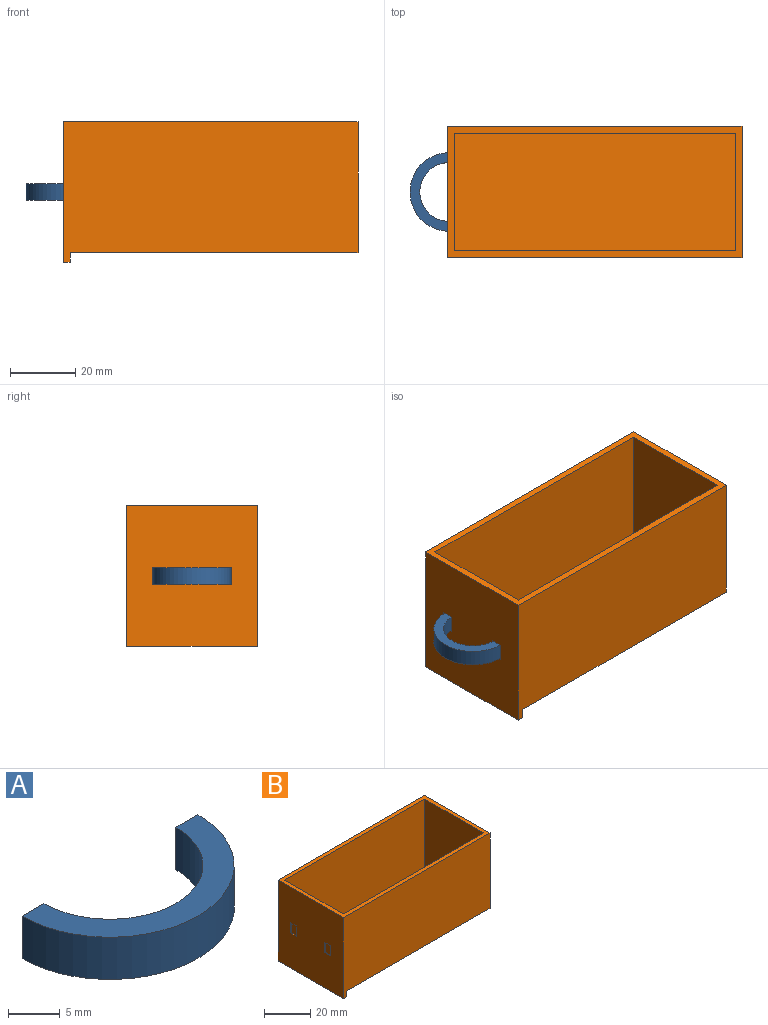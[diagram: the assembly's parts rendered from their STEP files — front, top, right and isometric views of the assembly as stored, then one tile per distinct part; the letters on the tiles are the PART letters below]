
ASSEMBLY  parts=2 mates=1
PART A: 6 faces, bbox 24x12x5 mm
  f0: plane 5x3mm, normal (0,1,0), area 15mm2, adj f1,f3,f4,f5
  f1: cylinder r=9mm len=18mm, axis (0,0,-1), area 141.4mm2, adj f0,f2,f4,f5
  f2: plane 5x3mm, normal (0,1,0), area 15mm2, adj f1,f3,f4,f5
  f3: cylinder r=12mm len=24mm, axis (0,0,-1), area 188.5mm2, adj f0,f2,f4,f5
  f4: plane 24x12mm, normal (0,0,1), area 99mm2, adj f0,f1,f2,f3
  f5: plane 24x12mm, normal (0,0,-1), area 99mm2, adj f0,f1,f2,f3
PART B: 23 faces, bbox 90x40x43 mm
  f0: plane 43x40mm, normal (-1,0,0), area 1683.3mm2, adj f2,f3,f4,f12,f13,f14,f15,f16
  f1: plane 88x40mm, normal (0,0,-1), area 3520mm2, adj f3,f4,f5,f11
  f2: plane 90x40mm, normal (0,0,1), area 504mm2, adj f0,f3,f4,f5,f6,f7,f8,f9
  f3: plane 90x43mm, normal (0,1,0), area 3606mm2, adj f0,f1,f2,f5,f11,f12
  f4: plane 90x43mm, normal (0,-1,0), area 3606mm2, adj f0,f1,f2,f5,f11,f12
  f5: plane 40x40mm, normal (1,0,0), area 1600mm2, adj f1,f2,f3,f4
  f6: plane 86x38mm, normal (0,-1,0), area 3268mm2, adj f2,f7,f9,f10
  f7: plane 38x36mm, normal (1,0,0), area 1368mm2, adj f2,f6,f8,f10
  f8: plane 86x38mm, normal (0,1,0), area 3268mm2, adj f2,f7,f9,f10
  f9: plane 38x36mm, normal (-1,0,0), area 1368mm2, adj f2,f6,f8,f10
  f10: plane 86x36mm, normal (0,0,1), area 3096mm2, adj f6,f7,f8,f9
  f11: plane 40x3mm, normal (1,0,0), area 120mm2, adj f1,f3,f4,f12
  f12: plane 40x2mm, normal (0,0,-1), area 80mm2, adj f0,f3,f4,f11
  f13: plane 3.4x0.5mm, normal (0,0,-1), area 1.7mm2, adj f0,f14,f16,f17
  f14: plane 5.4x0.5mm, normal (0,-1,0), area 2.7mm2, adj f0,f13,f15,f17
  f15: plane 3.4x0.5mm, normal (0,0,1), area 1.7mm2, adj f0,f14,f16,f17
  f16: plane 5.4x0.5mm, normal (0,1,0), area 2.7mm2, adj f0,f13,f15,f17
  f17: plane 5.4x3.4mm, normal (-1,0,0), area 18.4mm2, adj f13,f14,f15,f16
  f18: plane 3.4x0.5mm, normal (0,0,-1), area 1.7mm2, adj f0,f19,f21,f22
  f19: plane 5.4x0.5mm, normal (0,-1,0), area 2.7mm2, adj f0,f18,f20,f22
  f20: plane 3.4x0.5mm, normal (0,0,1), area 1.7mm2, adj f0,f19,f21,f22
  f21: plane 5.4x0.5mm, normal (0,1,0), area 2.7mm2, adj f0,f18,f20,f22
  f22: plane 5.4x3.4mm, normal (-1,0,0), area 18.4mm2, adj f18,f19,f20,f21
PLACE A rot(axis=(0,0,-1),90deg) t=(-313.81,259.31,16)mm
PLACE B t=(0,-0.1,0)mm
MATE fastened A.f0 <-> B.f17  axis (1,0,0) through (-323.02,149.91,18.5)mm
